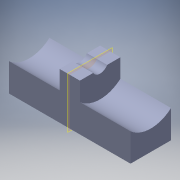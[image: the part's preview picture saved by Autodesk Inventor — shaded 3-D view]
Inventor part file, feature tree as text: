
AUTODESK INVENTOR PART (.ipt)
format: ipt  version: 2016 (Build 200138000, 138)  size: 126,464 bytes
history: native  units: in
note: dims shown in document units (in); Inventor stores cm internally (conversion verified against a paired STEP export)
features: other x2, plane x1, imported_body x1
ambient origin geometry x8: Origin, YZ Plane, XZ Plane, XY Plane, X Axis, Y Axis, Z Axis, Center Point
bodies: Body1 (feature_tree)
feature tree (4):
  other  "Cut-Extrude2"
  other  "sampleholder1"
  plane  "Work Plane1"
  imported_body  "Base1"
